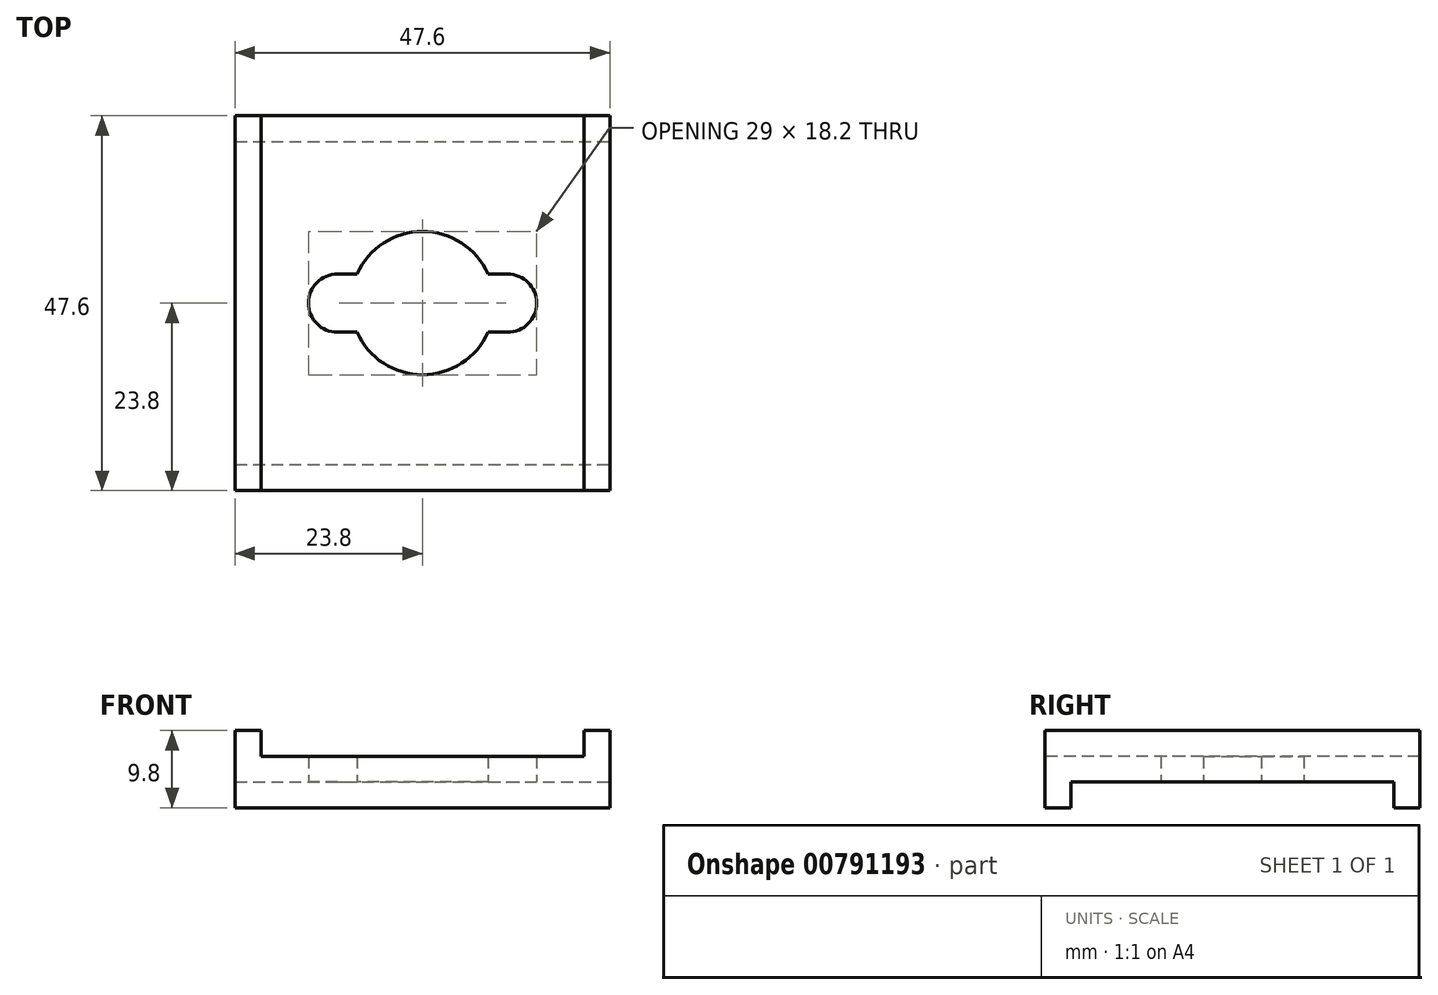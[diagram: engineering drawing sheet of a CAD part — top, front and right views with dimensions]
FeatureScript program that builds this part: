
annotation { "Feature Type Name" : "Feature", "Feature Type Description" : "" }
export const myFeature = defineFeature(function(context is Context, id is Id, definition is map)
    precondition{}
    {
        {
            var Q0;
            Q0=qCreatedBy(makeId("Top.planeOp"),FACE);
            var sketch = newSketch(context, id + "F0", { "sketchPlane" : qUnion([Q0])});
            skLineSegment(sketch, "E0.bottom", {"start": v(23.8, -23.8) * mm, "end": v(-23.8, -23.8) * mm});
            skLineSegment(sketch, "E0.top", {"start": v(23.8, 23.8) * mm, "end": v(-23.8, 23.8) * mm});
            skLineSegment(sketch, "E0.left", {"start": v(23.8, -23.8) * mm, "end": v(23.8, 23.8) * mm});
            skLineSegment(sketch, "E0.right", {"start": v(-23.8, -23.8) * mm, "end": v(-23.8, 23.8) * mm});
            skPoint(sketch, "E0.middle", {"position": v(0, 0) * mm});
            skArc(sketch, "E1", {"start": v(8.31, 3.7) * mm, "mid": v(0, 9.1) * mm, "end": v(-8.31, 3.7) * mm});
            skLineSegment(sketch, "E2", {"start": v(-10.8, 0) * mm, "end": v(10.8, 0) * mm, "construction": true});
            skArc(sketch, "E3.0.startCap", {"start": v(-10.8, -3.7) * mm, "mid": v(-14.5, 0) * mm, "end": v(-10.8, 3.7) * mm});
            skArc(sketch, "E3.0.endCap", {"start": v(10.8, 3.7) * mm, "mid": v(14.5, 0) * mm, "end": v(10.8, -3.7) * mm});
            skLineSegment(sketch, "E3.0.left", {"start": v(-10.8, 3.7) * mm, "end": v(-8.31, 3.7) * mm});
            skLineSegment(sketch, "E3.0.right", {"start": v(-10.8, -3.7) * mm, "end": v(-8.31, -3.7) * mm});
            skArc(sketch, "E4.trimOffspring", {"start": v(-8.31, -3.7) * mm, "mid": v(0, -9.1) * mm, "end": v(8.31, -3.7) * mm});
            skLineSegment(sketch, "E5.trimOffspring", {"start": v(8.31, 3.7) * mm, "end": v(10.8, 3.7) * mm});
            skLineSegment(sketch, "E6.trimOffspring", {"start": v(8.31, -3.7) * mm, "end": v(10.8, -3.7) * mm});
            skSolve(sketch);
        }
        {
            var Q0;
            Q0=makeQuery(id+"F0.imprint","IMPRINT",FACE,{"disambiguationData":[TD([[makeQuery(id+"F0.imprint","IMPRINT",EDGE,{"derivedFrom":sQuery(id+"F0.wireOp",EDGE,"E0.bottom")}),-1.0]])]});
            extrude(context, id + "F1", {"entities" : qUnion([Q0]), "endBound" : BoundingType.SYMMETRIC, "depth" : 3.2 * mm, "offsetDistance" : 25 * mm});
        }
        {
            var Q0;
            Q0=makeQuery(id+"F1.opExtrude","CAP_FACE",FACE,{"disambiguationData":[OSD([sQuery(id+"F0.wireOp",EDGE,"E0.bottom"),sQuery(id+"F0.wireOp",EDGE,"E0.top"),sQuery(id+"F0.wireOp",EDGE,"E0.left"),sQuery(id+"F0.wireOp",EDGE,"E0.right"),sQuery(id+"F0.wireOp",EDGE,"E1"),sQuery(id+"F0.wireOp",EDGE,"E3.0.startCap"),sQuery(id+"F0.wireOp",EDGE,"E3.0.endCap"),sQuery(id+"F0.wireOp",EDGE,"E3.0.left"),sQuery(id+"F0.wireOp",EDGE,"E3.0.right"),sQuery(id+"F0.wireOp",EDGE,"E4.trimOffspring"),sQuery(id+"F0.wireOp",EDGE,"E5.trimOffspring"),sQuery(id+"F0.wireOp",EDGE,"E6.trimOffspring")])],"isStart":false});
            var sketch = newSketch(context, id + "F2", { "sketchPlane" : qUnion([Q0])});
            skLineSegment(sketch, "E7.0.0", {"start": v(23.8, -23.8) * mm, "end": v(23.8, 23.8) * mm});
            skLineSegment(sketch, "E7.0.1", {"start": v(23.8, 23.8) * mm, "end": v(-23.8, 23.8) * mm});
            skLineSegment(sketch, "E7.0.2", {"start": v(-23.8, 23.8) * mm, "end": v(-23.8, -23.8) * mm});
            skLineSegment(sketch, "E7.0.3", {"start": v(-23.8, -23.8) * mm, "end": v(23.8, -23.8) * mm});
            skLineSegment(sketch, "E8", {"start": v(-20.5, 23.8) * mm, "end": v(-20.5, -23.8) * mm});
            skLineSegment(sketch, "E9", {"start": v(0, 0) * mm, "end": v(0, 6.16) * mm, "construction": true});
            skLineSegment(sketch, "E10.MirrorCS", {"start": v(20.5, 23.8) * mm, "end": v(20.5, -23.8) * mm});
            skSolve(sketch);
        }
        {
            var Q0;
            {var subQ0=sQuery(id+"F2.wireOp",EDGE,"E7.0.2");Q0=makeQuery(id+"F2.imprint","IMPRINT",FACE,{"disambiguationData":[TD([[makeQuery(id+"F2.imprint","IMPRINT",EDGE,{"derivedFrom":subQ0}),-1.0]])]});}
            var Q1;
            {var subQ0=sQuery(id+"F2.wireOp",EDGE,"E7.0.0");Q1=makeQuery(id+"F2.imprint","IMPRINT",FACE,{"disambiguationData":[TD([[makeQuery(id+"F2.imprint","IMPRINT",EDGE,{"derivedFrom":subQ0}),1.0]])]});}
            extrude(context, id + "F3", {"entities" : qUnion([Q0, Q1]), "operationType" : NewBodyOperationType.ADD, "depth" : 3.3 * mm, "offsetDistance" : 25 * mm});
        }
        {
            var Q0;
            Q0=makeQuery(id+"F1.opExtrude","CAP_FACE",FACE,{"disambiguationData":[OSD([sQuery(id+"F0.wireOp",EDGE,"E0.bottom"),sQuery(id+"F0.wireOp",EDGE,"E0.top"),sQuery(id+"F0.wireOp",EDGE,"E0.left"),sQuery(id+"F0.wireOp",EDGE,"E0.right"),sQuery(id+"F0.wireOp",EDGE,"E1"),sQuery(id+"F0.wireOp",EDGE,"E3.0.startCap"),sQuery(id+"F0.wireOp",EDGE,"E3.0.endCap"),sQuery(id+"F0.wireOp",EDGE,"E3.0.left"),sQuery(id+"F0.wireOp",EDGE,"E3.0.right"),sQuery(id+"F0.wireOp",EDGE,"E4.trimOffspring"),sQuery(id+"F0.wireOp",EDGE,"E5.trimOffspring"),sQuery(id+"F0.wireOp",EDGE,"E6.trimOffspring")])],"isStart":true});
            var sketch = newSketch(context, id + "F4", { "sketchPlane" : qUnion([Q0])});
            skLineSegment(sketch, "E11", {"start": v(-23.8, -20.5) * mm, "end": v(23.8, -20.5) * mm});
            skLineSegment(sketch, "E12", {"start": v(0, 0) * mm, "end": v(-10.8, 0) * mm, "construction": true});
            skLineSegment(sketch, "E13.MirrorCS", {"start": v(-23.8, 20.5) * mm, "end": v(23.8, 20.5) * mm});
            skSolve(sketch);
        }
        {
            var Q0;
            {var subQ0=sQuery(id+"F4.wireOp",EDGE,"E11");Q0=makeQuery(id+"F4.imprint","IMPRINT",FACE,{"disambiguationData":[TD([[makeQuery(id+"F4.imprint","IMPRINT",EDGE,{"derivedFrom":subQ0}),-1.0]])]});}
            var Q1;
            {var subQ0=sQuery(id+"F4.wireOp",EDGE,"E13.MirrorCS");Q1=makeQuery(id+"F4.imprint","IMPRINT",FACE,{"disambiguationData":[TD([[makeQuery(id+"F4.imprint","IMPRINT",EDGE,{"derivedFrom":subQ0}),1.0]])]});}
            extrude(context, id + "F5", {"entities" : qUnion([Q0, Q1]), "operationType" : NewBodyOperationType.ADD, "depth" : 3.3 * mm, "offsetDistance" : 25 * mm});
        }
    });
